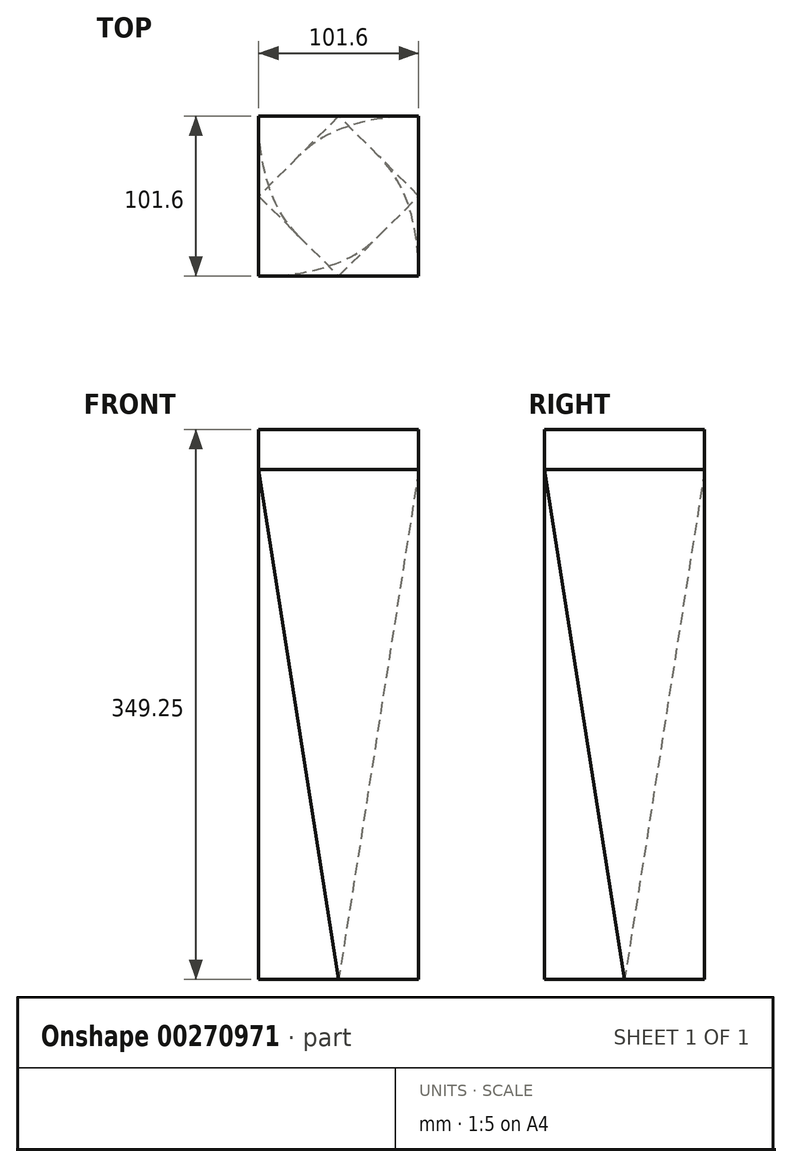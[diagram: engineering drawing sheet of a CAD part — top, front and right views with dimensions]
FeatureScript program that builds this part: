
annotation { "Feature Type Name" : "Feature", "Feature Type Description" : "" }
export const myFeature = defineFeature(function(context is Context, id is Id, definition is map)
    precondition{}
    {
        {
            var Q0;
            Q0=qCreatedBy(makeId("Front.planeOp"),FACE);
            var sketch = newSketch(context, id + "F0", { "sketchPlane" : qUnion([Q0])});
            skLineSegment(sketch, "E0", {"start": v(0, 0) * mm, "end": v(0, 25.4) * mm});
            skLineSegment(sketch, "E1", {"start": v(0, 25.4) * mm, "end": v(101.6, 25.4) * mm});
            skLineSegment(sketch, "E2", {"start": v(101.6, 25.4) * mm, "end": v(101.6, 0) * mm});
            skLineSegment(sketch, "E3", {"start": v(101.6, 0) * mm, "end": v(0, 0) * mm});
            skSolve(sketch);
        }
        {
            var Q0;
            Q0=makeQuery(id+"F0.imprint","IMPRINT",FACE,{"disambiguationData":[TD([[makeQuery(id+"F0.imprint","IMPRINT",EDGE,{"derivedFrom":sQuery(id+"F0.wireOp",EDGE,"E0")}),-1.0]])]});
            extrude(context, id + "F1", {"entities" : qUnion([Q0]), "depth" : 101.6 * mm});
        }
        {
            var Q0;
            Q0=makeQuery(id+"F1.opExtrude","SWEPT_FACE",FACE,{"disambiguationData":[OSD([sQuery(id+"F0.wireOp",EDGE,"E3")])]});
            cPlane(context, id + "F2", {"entities" : qUnion([Q0]), "cplaneType" : CPlaneType.OFFSET, "offset" : 323.85 * mm, "width" : 152.4 * mm, "height" : 152.4 * mm});
        }
        {
            var Q0;
            Q0=qCreatedBy(id+"F2.planeOp",FACE);
            var sketch = newSketch(context, id + "F3", { "sketchPlane" : qUnion([Q0])});
            skPoint(sketch, "E4.0", {"position": v(0, 50.8) * mm});
            skLineSegment(sketch, "E5", {"start": v(50.8, 0) * mm, "end": v(0, 50.8) * mm});
            skLineSegment(sketch, "E6", {"start": v(0, 50.8) * mm, "end": v(50.8, 101.6) * mm});
            skLineSegment(sketch, "E7", {"start": v(50.8, 101.6) * mm, "end": v(101.6, 50.8) * mm});
            skLineSegment(sketch, "E8", {"start": v(101.6, 50.8) * mm, "end": v(50.8, 0) * mm});
            skSolve(sketch);
        }
        {
            var Q1;
            Q1=makeQuery(id+"F1.opExtrude","SWEPT_FACE",FACE,{"disambiguationData":[OSD([sQuery(id+"F0.wireOp",EDGE,"E3")])]});
            var Q2;
            Q2=makeQuery(id+"F3.imprint","IMPRINT",FACE,{"disambiguationData":[TD([[makeQuery(id+"F3.imprint","IMPRINT",EDGE,{"derivedFrom":sQuery(id+"F3.wireOp",EDGE,"E5")}),-1.0]])]});
            loft(context, id + "F4", {"operationType" : NewBodyOperationType.ADD, "sheetProfilesArray" : [{ "sheetProfileEntities" : qUnion([Q1]) }, { "sheetProfileEntities" : qUnion([Q2]) }]});
        }
    });
